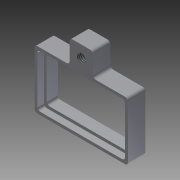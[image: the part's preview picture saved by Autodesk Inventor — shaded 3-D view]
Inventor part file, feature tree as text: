
AUTODESK INVENTOR PART (.ipt)
format: ipt  version: 2011 (Build 150239000, 239)  size: 164,352 bytes
history: native  units: in
note: dims shown in document units (in); Inventor stores cm internally (conversion verified against a paired STEP export)
features: sketch x6, extrude x5, hole x1, thread x1, fillet x1
ambient origin geometry x8: Origin, YZ Plane, XZ Plane, XY Plane, X Axis, Y Axis, Z Axis, Center Point
bodies: Solid1 (feature_tree)
feature tree (14):
  extrude  "Extrusion1"  Depth=0.3937in
  extrude  "Extrusion2"  Depth=0.5512in
  extrude  "Extrusion3"  Depth=0.1181in TaperAngle=0.0deg
  extrude  "Extrusion4"  Depth=0.2362in
  hole  "Hole1"  [1 undecoded]
  thread  "Thread1"  [1 undecoded]
  extrude  "Extrusion5"  Depth=1.0in TaperAngle=0.0deg
  fillet  "Fillet1"  Radius=0.0787in
  sketch  "Sketch1"  dims[d0=0.6299in d1=0.3937in]
  sketch  "Sketch2"  dims[d2=0.1181in d3=0.0in d4=0.5512in]
  sketch  "Sketch3"  dims[d5=0.315in d6=0.1181in d7=0.0in]
  sketch  "Sketch5"  dims[d13=0.1575in d14=0.2362in]
  sketch  "Sketch6"  dims[d15=0.1575in d16=0.0in d17=0.0197in d18=0.0433in d19=0.0in]
  sketch  "Sketch7"  dims[d20=0.06in d21=0.75in d22=0.375in d23=0.25in d24=0.5635in d25=0.07in d26=0.8108in d27=1.0in d28=0.0in d29=0.0787in d30=0.0394in d31=0.2756in d32=0.0394in d33=0.0in d34=0.0197in]
note: 2 required parameter values undecoded (feature->parameter linkage not recoverable at this tier; creation-order binding heuristic only, values carry confidence <= 0.55)
